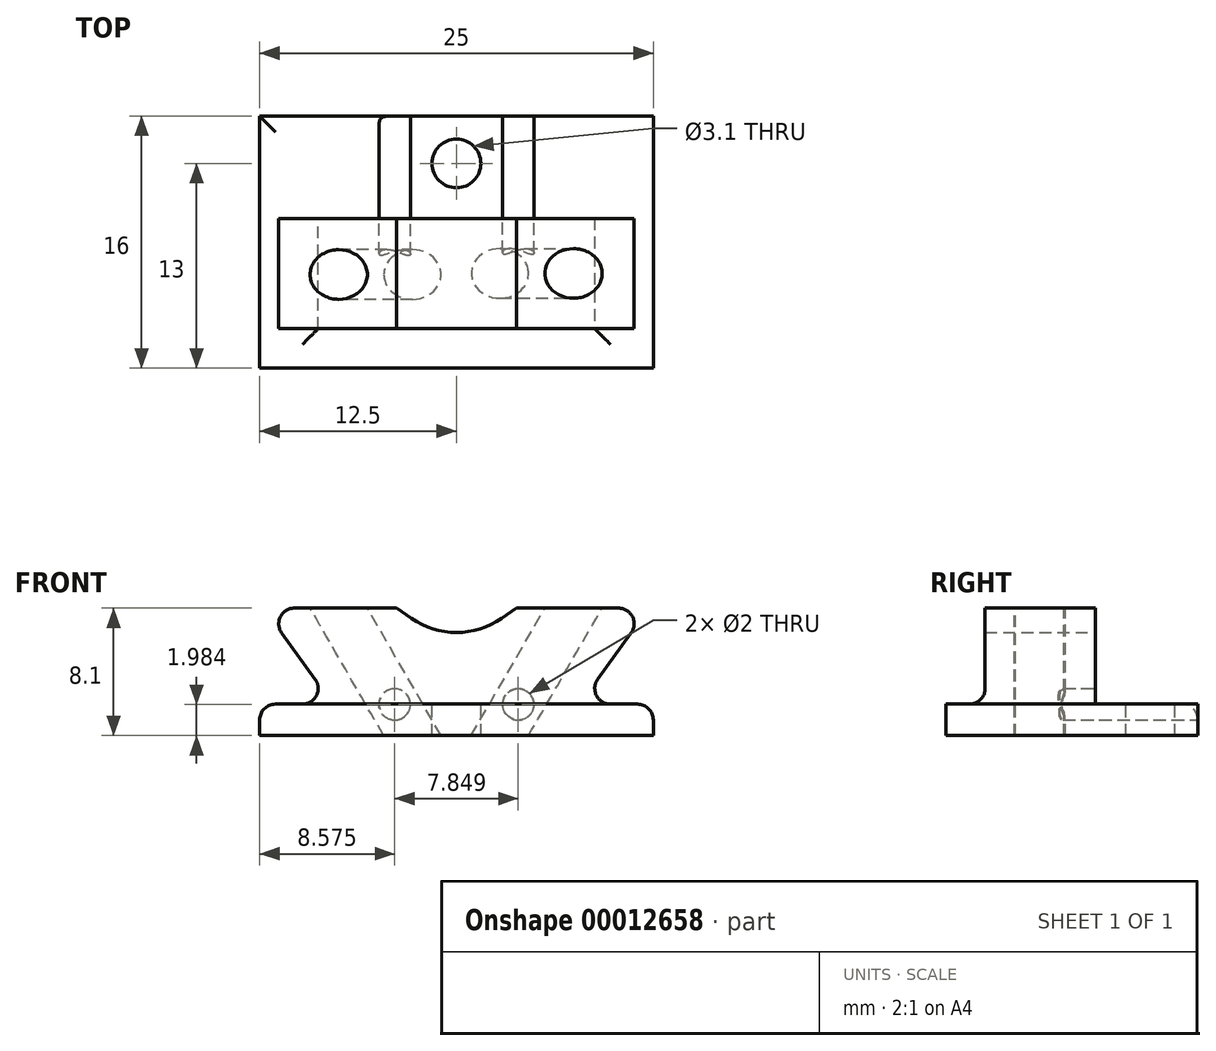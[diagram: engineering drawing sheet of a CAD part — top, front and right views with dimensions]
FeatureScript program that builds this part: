
annotation { "Feature Type Name" : "Feature", "Feature Type Description" : "" }
export const myFeature = defineFeature(function(context is Context, id is Id, definition is map)
    precondition{}
    {
        {
            var Q0;
            Q0=qCreatedBy(makeId("Front.planeOp"),FACE);
            cPlane(context, id + "F0", {"entities" : qUnion([Q0]), "cplaneType" : CPlaneType.OFFSET, "offset" : 2 * mm, "width" : 150 * mm, "height" : 150 * mm});
        }
        {
            var Q0;
            Q0=qCreatedBy(makeId("Top.planeOp"),FACE);
            var sketch = newSketch(context, id + "F1", { "sketchPlane" : qUnion([Q0])});
            skLineSegment(sketch, "E0.rect.bottom", {"start": v(12.5, -8) * mm, "end": v(-12.5, -8) * mm});
            skLineSegment(sketch, "E0.rect.top", {"start": v(12.5, 8) * mm, "end": v(-12.5, 8) * mm});
            skLineSegment(sketch, "E0.rect.left", {"start": v(12.5, -8) * mm, "end": v(12.5, 8) * mm});
            skLineSegment(sketch, "E0.rect.right", {"start": v(-12.5, -8) * mm, "end": v(-12.5, 8) * mm});
            skPoint(sketch, "E0.rect.middle", {"position": v(0, 0) * mm});
            skSolve(sketch);
        }
        {
            var Q0;
            Q0=makeQuery(id+"F1.imprint","IMPRINT",FACE,{"disambiguationData":[TD([[makeQuery(id+"F1.imprint","IMPRINT",EDGE,{"derivedFrom":sQuery(id+"F1.wireOp",EDGE,"E0.rect.bottom")}),-1.0]])]});
            extrude(context, id + "F2", {"entities" : qUnion([Q0]), "depth" : 2 * mm});
        }
        {
            var Q0;
            Q0=makeQuery(id+"F2.opExtrude","CAP_FACE",FACE,{"disambiguationData":[OSD([sQuery(id+"F1.wireOp",EDGE,"E0.rect.bottom"),sQuery(id+"F1.wireOp",EDGE,"E0.rect.top"),sQuery(id+"F1.wireOp",EDGE,"E0.rect.left"),sQuery(id+"F1.wireOp",EDGE,"E0.rect.right")])],"isStart":false});
            var sketch = newSketch(context, id + "F3", { "sketchPlane" : qUnion([Q0])});
            skLineSegment(sketch, "E1", {"start": v(-17.25, 5) * mm, "end": v(20.16, 5) * mm, "construction": true});
            skCircle(sketch, "E2", {"center": v(0, 5) * mm, "radius": 1.55 * mm});
            skSolve(sketch);
        }
        {
            var Q0;
            Q0=makeQuery(id+"F3.imprint","IMPRINT",FACE,{"disambiguationData":[TD([[makeQuery(id+"F3.imprint","IMPRINT",EDGE,{"derivedFrom":sQuery(id+"F3.wireOp",EDGE,"E2")}),1.0]])]});
            extrude(context, id + "F4", {"entities" : qUnion([Q0]), "operationType" : NewBodyOperationType.REMOVE, "endBound" : BoundingType.THROUGH_ALL, "oppositeDirection" : true, "depth" : 25 * mm});
        }
        {
            var Q0;
            Q0=qCreatedBy(id+"F0.planeOp",FACE);
            var sketch = newSketch(context, id + "F5", { "sketchPlane" : qUnion([Q0])});
            skLineSegment(sketch, "E3", {"start": v(-12.25, 8.1) * mm, "end": v(-3.8, 8.1) * mm});
            skLineSegment(sketch, "E4", {"start": v(-3.8, 8.1) * mm, "end": v(-2.87, 7.45) * mm});
            skLineSegment(sketch, "E5", {"start": v(2.87, 7.45) * mm, "end": v(3.8, 8.1) * mm});
            skLineSegment(sketch, "E6", {"start": v(3.8, 8.1) * mm, "end": v(12.25, 8.1) * mm});
            skLineSegment(sketch, "E7", {"start": v(-12.25, 8.1) * mm, "end": v(-6.37, 0) * mm});
            skLineSegment(sketch, "E8", {"start": v(6.37, 0) * mm, "end": v(12.25, 8.1) * mm});
            skLineSegment(sketch, "E9", {"start": v(-6.37, 0) * mm, "end": v(6.37, 0) * mm});
            skPoint(sketch, "E10.orphan", {"position": v(0, -8.79) * mm});
            skPoint(sketch, "E11.visualSharp", {"position": v(0, 5.44) * mm});
            skArc(sketch, "E11.filletArc", {"start": v(-2.87, 7.45) * mm, "mid": v(0, 6.55) * mm, "end": v(2.87, 7.45) * mm});
            skSolve(sketch);
        }
        {
            var Q0;
            Q0 = qSketchRegion(id + "F5", true);
            extrude(context, id + "F6", {"entities" : qUnion([Q0]), "operationType" : NewBodyOperationType.ADD, "endBound" : BoundingType.SYMMETRIC, "depth" : 7 * mm});
        }
        {
            var Q0;
            Q0=qCreatedBy(id+"F0.planeOp",FACE);
            var sketch = newSketch(context, id + "F7", { "sketchPlane" : qUnion([Q0])});
            skLineSegment(sketch, "E12", {"start": v(-10, 12.55) * mm, "end": v(0, -4.77) * mm, "construction": true});
            skLineSegment(sketch, "E13", {"start": v(0, -4.77) * mm, "end": v(10, 12.55) * mm, "construction": true});
            skLineSegment(sketch, "E14", {"start": v(10, 12.55) * mm, "end": v(-10, 12.55) * mm, "construction": true});
            skSolve(sketch);
        }
        {
            var Q0;
            Q0=sQuery(id+"F7.wireOp",VERTEX,"E14.start");
            var Q1;
            Q1=sQuery(id+"F7.wireOp",EDGE,"E13");
            cPlane(context, id + "F8", {"entities" : qUnion([Q0, Q1]), "cplaneType" : CPlaneType.LINE_POINT, "offset" : 150 * mm, "width" : 150 * mm, "height" : 150 * mm});
        }
        {
            var Q0;
            Q0=qCreatedBy(id+"F8.planeOp",FACE);
            var sketch = newSketch(context, id + "F9", { "sketchPlane" : qUnion([Q0])});
            skCircle(sketch, "E15", {"center": v(2.39, -2) * mm, "radius": 1.57 * mm});
            skSolve(sketch);
        }
        {
            var Q0;
            Q0 = qSketchRegion(id + "F9", true);
            extrude(context, id + "F10", {"entities" : qUnion([Q0]), "operationType" : NewBodyOperationType.REMOVE, "oppositeDirection" : true, "depth" : 25 * mm});
        }
        {
            var Q0;
            Q0=sQuery(id+"F7.wireOp",EDGE,"E12");
            var Q1;
            Q1=sQuery(id+"F7.wireOp",VERTEX,"E14.end");
            cPlane(context, id + "F11", {"entities" : qUnion([Q0, Q1]), "cplaneType" : CPlaneType.LINE_POINT, "offset" : 150 * mm, "width" : 150 * mm, "height" : 150 * mm});
        }
        {
            var Q0;
            Q0=qCreatedBy(id+"F11.planeOp",FACE);
            var sketch = newSketch(context, id + "F12", { "sketchPlane" : qUnion([Q0])});
            skCircle(sketch, "E16", {"center": v(-2.42, 2.06) * mm, "radius": 1.57 * mm});
            skSolve(sketch);
        }
        {
            var Q0;
            Q0 = qSketchRegion(id + "F12", true);
            extrude(context, id + "F13", {"entities" : qUnion([Q0]), "operationType" : NewBodyOperationType.REMOVE, "endBound" : BoundingType.THROUGH_ALL, "depth" : 25 * mm});
        }
        {
            var Q0;
            Q0=makeQuery(id+"F2.opExtrude","SWEPT_FACE",FACE,{"disambiguationData":[OSD([sQuery(id+"F1.wireOp",EDGE,"E0.rect.top")])]});
            var sketch = newSketch(context, id + "F14", { "sketchPlane" : qUnion([Q0])});
            skCircle(sketch, "E17", {"center": v(3.92, 1.98) * mm, "radius": 1 * mm});
            skCircle(sketch, "E18.0.MirrorC", {"center": v(-3.92, 1.98) * mm, "radius": 1 * mm});
            skSolve(sketch);
        }
        {
            var Q0;
            Q0 = qSketchRegion(id + "F14", true);
            var Q1;
            Q1=qCreatedBy(id+"F0.planeOp",FACE);
            extrude(context, id + "F15", {"entities" : qUnion([Q0]), "operationType" : NewBodyOperationType.REMOVE, "endBound" : BoundingType.UP_TO_SURFACE, "oppositeDirection" : true, "endBoundEntityFace" : qUnion([Q1]), "depth" : 25 * mm});
        }
        {
            var Q0;
            Q0=makeQuery(id+"F6.boolean.opBoolean","INTERSECT",EDGE,{"derivedFrom":[makeQuery(id+"F2.opExtrude","CAP_FACE",FACE,{"disambiguationData":[OSD([sQuery(id+"F1.wireOp",EDGE,"E0.rect.bottom"),sQuery(id+"F1.wireOp",EDGE,"E0.rect.top"),sQuery(id+"F1.wireOp",EDGE,"E0.rect.left"),sQuery(id+"F1.wireOp",EDGE,"E0.rect.right")])],"isStart":false}),makeQuery(id+"F6.opExtrude","CAP_FACE",FACE,{"disambiguationData":[OSD([sQuery(id+"F5.wireOp",EDGE,"E3"),sQuery(id+"F5.wireOp",EDGE,"E4"),sQuery(id+"F5.wireOp",EDGE,"E5"),sQuery(id+"F5.wireOp",EDGE,"E6"),sQuery(id+"F5.wireOp",EDGE,"E7"),sQuery(id+"F5.wireOp",EDGE,"E8"),sQuery(id+"F5.wireOp",EDGE,"E9"),sQuery(id+"F5.wireOp",EDGE,"E11.filletArc")])],"isStart":false})]});
            var Q1;
            Q1=makeQuery(id+"F6.boolean.opBoolean","INTERSECT",EDGE,{"derivedFrom":[makeQuery(id+"F2.opExtrude","CAP_FACE",FACE,{"disambiguationData":[OSD([sQuery(id+"F1.wireOp",EDGE,"E0.rect.bottom"),sQuery(id+"F1.wireOp",EDGE,"E0.rect.top"),sQuery(id+"F1.wireOp",EDGE,"E0.rect.left"),sQuery(id+"F1.wireOp",EDGE,"E0.rect.right")])],"isStart":false}),makeQuery(id+"F6.opExtrude","SWEPT_FACE",FACE,{"disambiguationData":[OSD([sQuery(id+"F5.wireOp",EDGE,"E8")])]})]});
            var Q2;
            Q2=makeQuery(id+"F6.boolean.opBoolean","INTERSECT",EDGE,{"derivedFrom":[makeQuery(id+"F2.opExtrude","CAP_FACE",FACE,{"disambiguationData":[OSD([sQuery(id+"F1.wireOp",EDGE,"E0.rect.bottom"),sQuery(id+"F1.wireOp",EDGE,"E0.rect.top"),sQuery(id+"F1.wireOp",EDGE,"E0.rect.left"),sQuery(id+"F1.wireOp",EDGE,"E0.rect.right")])],"isStart":false}),makeQuery(id+"F6.opExtrude","SWEPT_FACE",FACE,{"disambiguationData":[OSD([sQuery(id+"F5.wireOp",EDGE,"E7")])]})]});
            var Q3;
            Q3=makeQuery(id+"F6.opExtrude","SWEPT_EDGE",EDGE,{"disambiguationData":[OSD([sQuery(id+"F5.wireOp",EDGE,"E6"),sQuery(id+"F5.wireOp",EDGE,"E8")])]});
            var Q4;
            Q4=makeQuery(id+"F6.opExtrude","SWEPT_EDGE",EDGE,{"disambiguationData":[OSD([sQuery(id+"F5.wireOp",EDGE,"E3"),sQuery(id+"F5.wireOp",EDGE,"E7")])]});
            var Q5;
            Q5=makeQuery(id+"F2.opExtrude","CAP_EDGE",EDGE,{"disambiguationData":[OSD([sQuery(id+"F1.wireOp",EDGE,"E0.rect.left")])],"isStart":false});
            var Q6;
            Q6=makeQuery(id+"F2.opExtrude","CAP_EDGE",EDGE,{"disambiguationData":[OSD([sQuery(id+"F1.wireOp",EDGE,"E0.rect.right")])],"isStart":false});
            var Q7;
            {var subQ0=sQuery(id+"F1.wireOp",EDGE,"E0.rect.top");var subQ1=sQuery(id+"F1.wireOp",EDGE,"E0.rect.right");Q7=makeQuery(id+"F15.boolean.opBoolean","SPLIT",EDGE,{"disambiguationData":[TD([makeQuery(id+"F2.opExtrude","CAP_FACE",FACE,{"disambiguationData":[OSD([sQuery(id+"F1.wireOp",EDGE,"E0.rect.bottom"),subQ0,sQuery(id+"F1.wireOp",EDGE,"E0.rect.left"),subQ1])],"isStart":false}),makeQuery(id+"F2.opExtrude","SWEPT_FACE",FACE,{"disambiguationData":[OSD([subQ0])]}),makeQuery(id+"F2.opExtrude","SWEPT_FACE",FACE,{"disambiguationData":[OSD([subQ1])]}),makeQuery(id+"F15.opExtrude","SWEPT_FACE",FACE,{"disambiguationData":[OSD([sQuery(id+"F14.wireOp",EDGE,"E17")])]})])],"derivedFrom":makeQuery(id+"F2.opExtrude","CAP_EDGE",EDGE,{"disambiguationData":[OSD([subQ0])],"isStart":false})});}
            fillet(context, id + "F16", {"entities" : qUnion([Q0, Q1, Q2, Q3, Q4, Q5, Q6, Q7]), "radius" : 1 * mm, "tangentPropagation" : true, "allowEdgeOverflow" : false});
        }
    });
